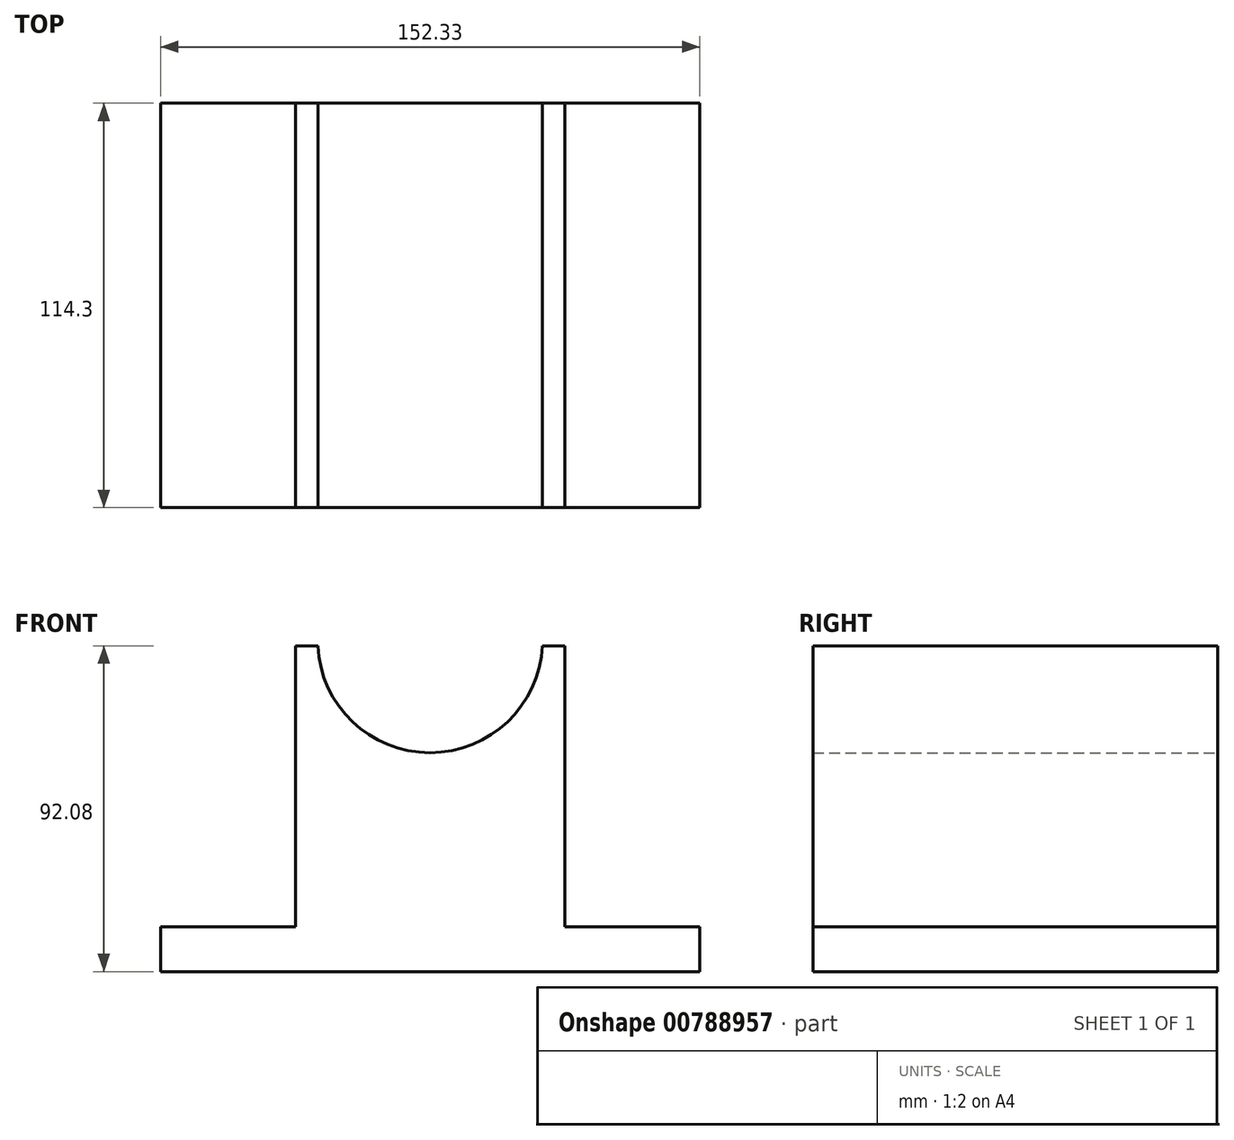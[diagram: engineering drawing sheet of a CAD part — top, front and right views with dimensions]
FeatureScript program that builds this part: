
annotation { "Feature Type Name" : "Feature", "Feature Type Description" : "" }
export const myFeature = defineFeature(function(context is Context, id is Id, definition is map)
    precondition{}
    {
        {
            var Q0;
            Q0=qCreatedBy(makeId("Front.planeOp"),FACE);
            var sketch = newSketch(context, id + "F0", { "sketchPlane" : qUnion([Q0])});
            skLineSegment(sketch, "E0", {"start": v(0, 0) * mm, "end": v(0, 12.7) * mm});
            skLineSegment(sketch, "E1", {"start": v(0, 12.7) * mm, "end": v(38.1, 12.7) * mm});
            skLineSegment(sketch, "E2", {"start": v(38.1, 12.7) * mm, "end": v(38.1, 92.08) * mm});
            skLineSegment(sketch, "E3", {"start": v(114.23, 92.08) * mm, "end": v(114.23, 12.7) * mm});
            skLineSegment(sketch, "E4", {"start": v(114.23, 12.7) * mm, "end": v(152.33, 12.7) * mm});
            skLineSegment(sketch, "E5", {"start": v(152.33, 12.7) * mm, "end": v(152.33, 0) * mm});
            skLineSegment(sketch, "E6", {"start": v(152.33, 0) * mm, "end": v(0, 0) * mm});
            skLineSegment(sketch, "E7", {"start": v(38.1, 92.08) * mm, "end": v(44.45, 92.08) * mm});
            skLineSegment(sketch, "E8", {"start": v(114.23, 92.08) * mm, "end": v(107.88, 92.08) * mm});
            skArc(sketch, "E9", {"start": v(44.45, 92.08) * mm, "mid": v(76.16, 61.84) * mm, "end": v(107.88, 92.08) * mm});
            skSolve(sketch);
        }
        {
            var Q0;
            Q0 = qSketchRegion(id + "F0", true);
            extrude(context, id + "F1", {"entities" : qUnion([Q0]), "depth" : 114.3 * mm, "offsetDistance" : 25.4 * mm});
        }
    });
